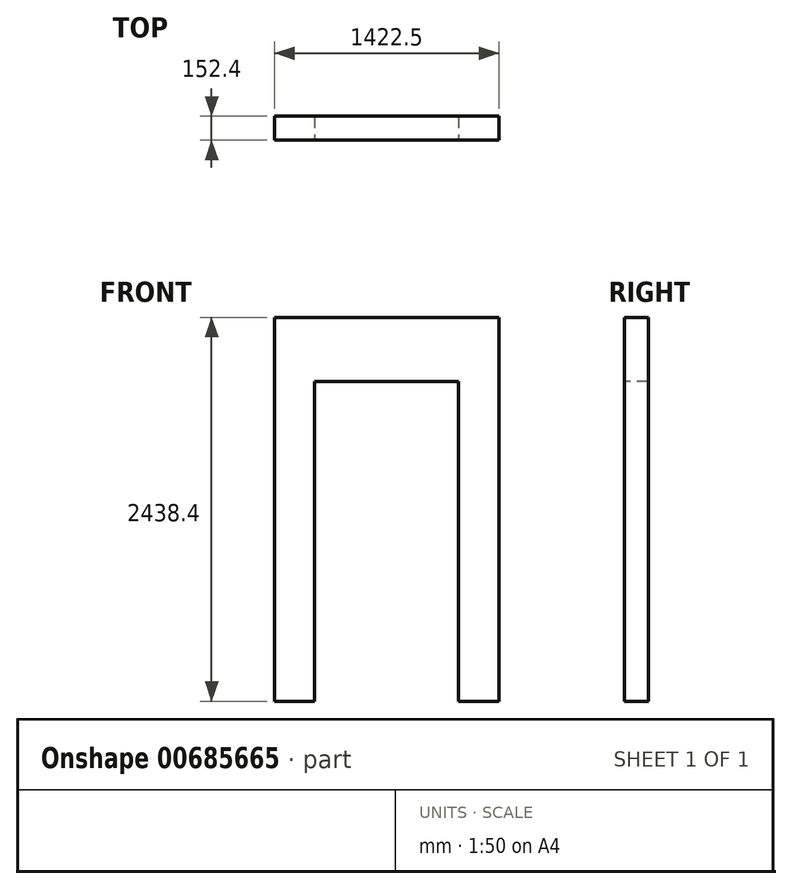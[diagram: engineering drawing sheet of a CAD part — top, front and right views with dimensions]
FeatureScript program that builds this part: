
annotation { "Feature Type Name" : "Feature", "Feature Type Description" : "" }
export const myFeature = defineFeature(function(context is Context, id is Id, definition is map)
    precondition{}
    {
        {
            var Q0;
            Q0=qCreatedBy(makeId("Top.planeOp"),FACE);
            var sketch = newSketch(context, id + "F0", { "sketchPlane" : qUnion([Q0])});
            skLineSegment(sketch, "E0.bottom", {"start": v(0, 0) * mm, "end": v(1422.5, 0) * mm});
            skLineSegment(sketch, "E0.top", {"start": v(0, 152.4) * mm, "end": v(1422.5, 152.4) * mm});
            skLineSegment(sketch, "E0.left", {"start": v(0, 0) * mm, "end": v(0, 152.4) * mm});
            skLineSegment(sketch, "E0.right", {"start": v(1422.5, 0) * mm, "end": v(1422.5, 152.4) * mm});
            skSolve(sketch);
        }
        {
            var Q0;
            Q0 = qSketchRegion(id + "F0", true);
            extrude(context, id + "F1", {"entities" : qUnion([Q0]), "depth" : 2438.4 * mm, "offsetDistance" : 30.48 * mm});
        }
        {
            var Q0;
            Q0=makeQuery(id+"F1.opExtrude","SWEPT_FACE",FACE,{"disambiguationData":[OSD([sQuery(id+"F0.wireOp",EDGE,"E0.bottom")])]});
            var sketch = newSketch(context, id + "F2", { "sketchPlane" : qUnion([Q0])});
            skLineSegment(sketch, "E1.bottom", {"start": v(254.05, 0) * mm, "end": v(1168.45, 0) * mm});
            skLineSegment(sketch, "E1.top", {"start": v(254.05, 2032.1) * mm, "end": v(1168.45, 2032.1) * mm});
            skLineSegment(sketch, "E1.left", {"start": v(254.05, 0) * mm, "end": v(254.05, 2032.1) * mm});
            skLineSegment(sketch, "E1.right", {"start": v(1168.45, 0) * mm, "end": v(1168.45, 2032.1) * mm});
            skLineSegment(sketch, "E2", {"start": v(711.25, 2438.4) * mm, "end": v(711.25, 0) * mm, "construction": true});
            skPoint(sketch, "E3", {"position": v(711.25, 2032.1) * mm});
            skSolve(sketch);
        }
        {
            var Q0;
            Q0 = qSketchRegion(id + "F2", true);
            extrude(context, id + "F3", {"entities" : qUnion([Q0]), "operationType" : NewBodyOperationType.REMOVE, "endBound" : BoundingType.THROUGH_ALL, "oppositeDirection" : true, "depth" : 30.48 * mm, "offsetDistance" : 30.48 * mm});
        }
    });
